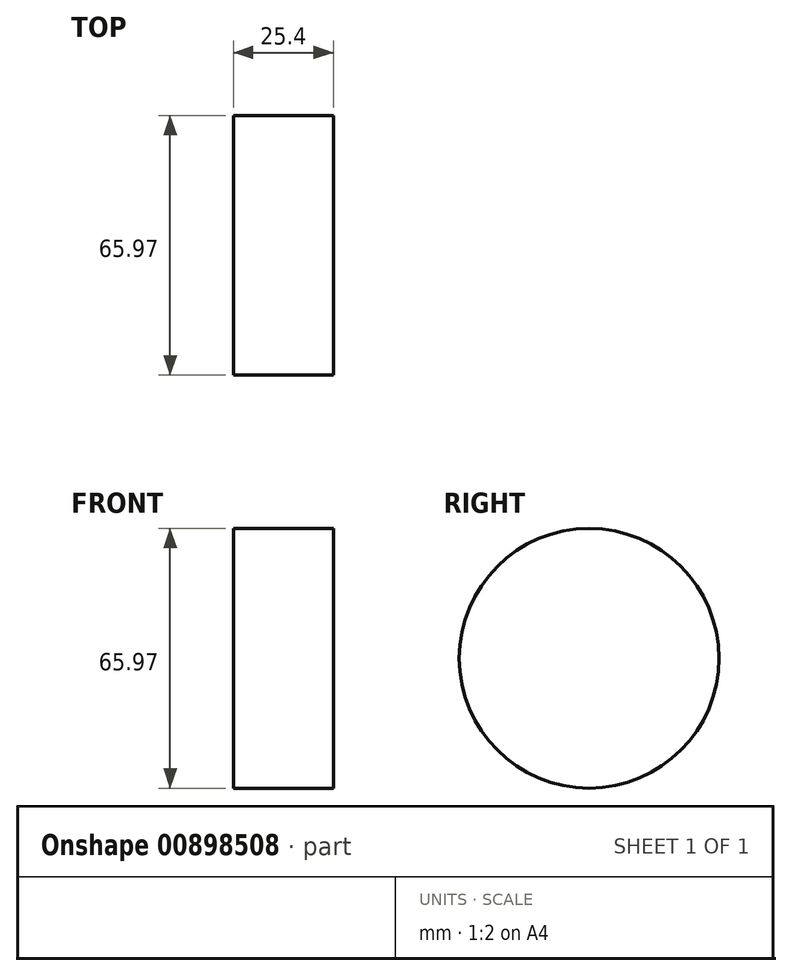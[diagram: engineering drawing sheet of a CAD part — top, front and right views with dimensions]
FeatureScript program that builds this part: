
annotation { "Feature Type Name" : "Feature", "Feature Type Description" : "" }
export const myFeature = defineFeature(function(context is Context, id is Id, definition is map)
    precondition{}
    {
        {
            var Q0;
            Q0=qCreatedBy(makeId("Right.planeOp"),FACE);
            var sketch = newSketch(context, id + "F0", { "sketchPlane" : qUnion([Q0])});
            skCircle(sketch, "E0", {"center": v(-14.23, 18.24) * mm, "radius": 32.99 * mm});
            skSolve(sketch);
        }
        {
            var Q0;
            Q0=makeQuery(id+"F0.imprint","IMPRINT",FACE,{"disambiguationData":[TD([[makeQuery(id+"F0.imprint","IMPRINT",EDGE,{"derivedFrom":sQuery(id+"F0.wireOp",EDGE,"E0")}),1.0]])]});
            extrude(context, id + "F1", {"entities" : qUnion([Q0]), "oppositeDirection" : true, "depth" : 25.4 * mm, "offsetDistance" : 25.4 * mm});
        }
    });
